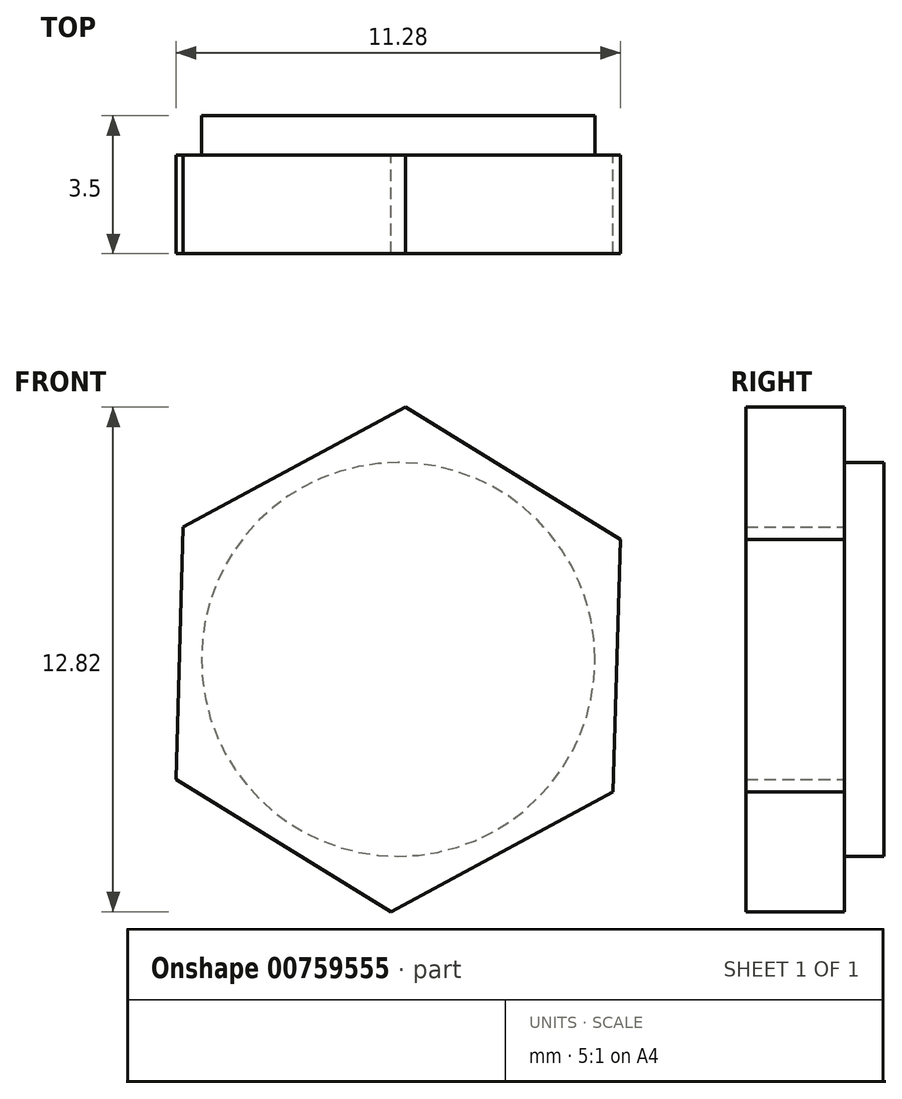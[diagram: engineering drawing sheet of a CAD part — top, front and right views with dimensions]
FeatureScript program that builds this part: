
annotation { "Feature Type Name" : "Feature", "Feature Type Description" : "" }
export const myFeature = defineFeature(function(context is Context, id is Id, definition is map)
    precondition{}
    {
        {
            var Q0;
            Q0=qCreatedBy(makeId("Front.planeOp"),FACE);
            var sketch = newSketch(context, id + "F0", { "sketchPlane" : qUnion([Q0])});
            skCircle(sketch, "E0.cCircle", {"center": v(0, 0) * mm, "radius": 5.55 * mm, "construction": true});
            skLineSegment(sketch, "E0.0", {"start": v(0.18, 6.41) * mm, "end": v(5.64, 3.05) * mm});
            skLineSegment(sketch, "E0.1", {"start": v(5.64, 3.05) * mm, "end": v(5.46, -3.36) * mm});
            skLineSegment(sketch, "E0.2", {"start": v(5.46, -3.36) * mm, "end": v(-0.18, -6.41) * mm});
            skLineSegment(sketch, "E0.3", {"start": v(-0.18, -6.41) * mm, "end": v(-5.64, -3.05) * mm});
            skLineSegment(sketch, "E0.4", {"start": v(-5.64, -3.05) * mm, "end": v(-5.46, 3.36) * mm});
            skLineSegment(sketch, "E0.5", {"start": v(-5.46, 3.36) * mm, "end": v(0.18, 6.41) * mm});
            skPoint(sketch, "E0.0.midPoint", {"position": v(2.91, 4.73) * mm});
            skSolve(sketch);
        }
        {
            var Q0;
            Q0 = qSketchRegion(id + "F0", true);
            extrude(context, id + "F1", {"entities" : qUnion([Q0]), "depth" : 2.5 * mm, "offsetDistance" : 25 * mm});
        }
        {
            var Q0;
            Q0=qCreatedBy(makeId("Front.planeOp"),FACE);
            var sketch = newSketch(context, id + "F2", { "sketchPlane" : qUnion([Q0])});
            skCircle(sketch, "E1", {"center": v(0, 0) * mm, "radius": 5 * mm});
            skSolve(sketch);
        }
        {
            var Q0;
            Q0 = qSketchRegion(id + "F2", true);
            extrude(context, id + "F3", {"entities" : qUnion([Q0]), "operationType" : NewBodyOperationType.ADD, "oppositeDirection" : true, "depth" : 1 * mm, "offsetDistance" : 25 * mm});
        }
    });
